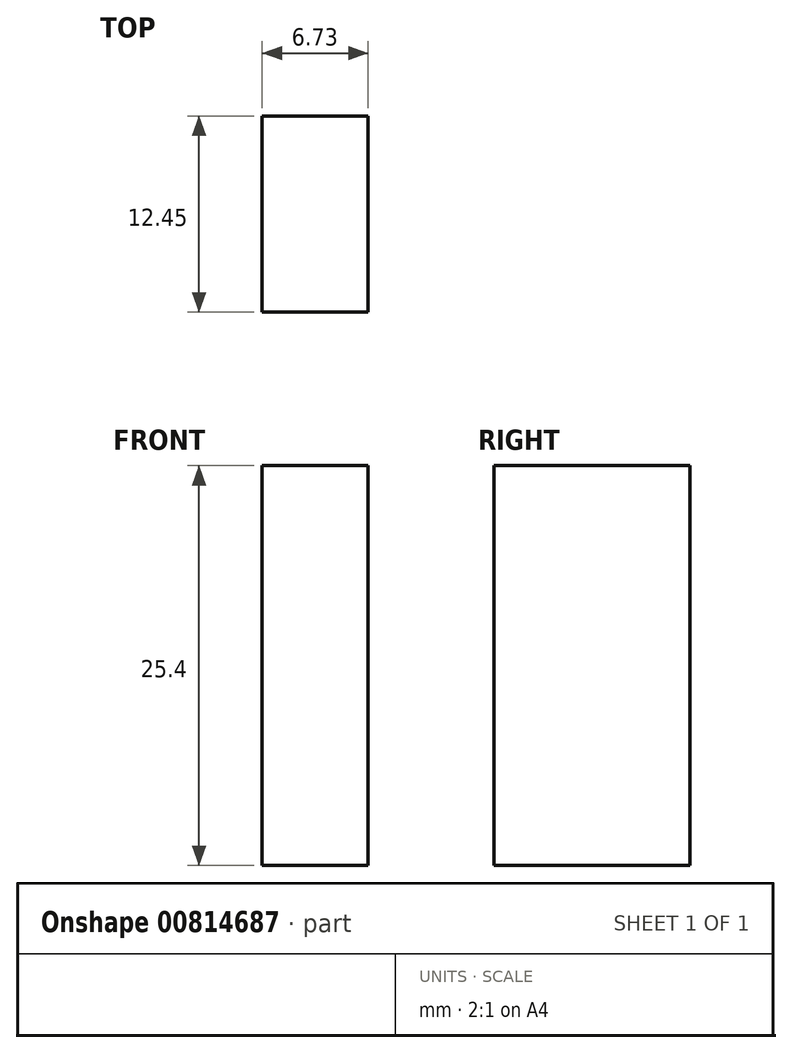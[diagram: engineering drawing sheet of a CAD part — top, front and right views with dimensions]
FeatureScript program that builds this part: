
annotation { "Feature Type Name" : "Feature", "Feature Type Description" : "" }
export const myFeature = defineFeature(function(context is Context, id is Id, definition is map)
    precondition{}
    {
        {
            var Q0;
            Q0=qCreatedBy(makeId("Top.planeOp"),FACE);
            var sketch = newSketch(context, id + "F0", { "sketchPlane" : qUnion([Q0])});
            skLineSegment(sketch, "E0.bottom", {"start": v(0, 0) * mm, "end": v(6.73, 0) * mm});
            skLineSegment(sketch, "E0.top", {"start": v(0, 12.45) * mm, "end": v(6.73, 12.45) * mm});
            skLineSegment(sketch, "E0.left", {"start": v(0, 0) * mm, "end": v(0, 12.45) * mm});
            skLineSegment(sketch, "E0.right", {"start": v(6.73, 0) * mm, "end": v(6.73, 12.45) * mm});
            skSolve(sketch);
        }
        {
            var Q0;
            Q0=makeQuery(id+"F0.imprint","IMPRINT",FACE,{"disambiguationData":[TD([[makeQuery(id+"F0.imprint","IMPRINT",EDGE,{"derivedFrom":sQuery(id+"F0.wireOp",EDGE,"E0.bottom")}),1.0]])]});
            extrude(context, id + "F1", {"entities" : qUnion([Q0]), "depth" : 25.4 * mm, "offsetDistance" : 25.4 * mm});
        }
    });
